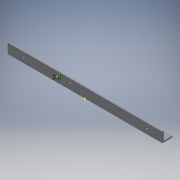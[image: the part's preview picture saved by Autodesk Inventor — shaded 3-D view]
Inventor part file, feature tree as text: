
AUTODESK INVENTOR PART (.ipt)
format: ipt  version: 2018 (Build 220112000, 112)  size: 144,896 bytes
history: native  units: mm
features: sketch x7, extrude x6, other x3, reference x2, projected_geometry x1
ambient origin geometry x8: Origin, YZ Plane, XZ Plane, XY Plane, X Axis, Y Axis, Z Axis, Center Point
bodies: Solid1 (feature_tree)
feature tree (19):
  extrude  "Extrusion1"  Depth=15.08mm
  extrude  "Extrusion2"  Depth=2.05mm
  extrude  "Extrusion3"  Depth=13.03mm
  sketch  "Sketch4"  dims[d8=93.5mm d9=8.0mm]
  extrude  "Extrusion5"  Depth=8.0mm
  extrude  "Extrusion6"  Depth=2.05mm TaperAngle=0.0deg
  extrude  "Extrusion7"  Depth=3.2mm
  sketch  "Sketch1"  dims[d0=234.5mm d1=15.08mm]
  sketch  "Sketch2"  dims[d2=2.05mm d3=0.0mm d4=2.05mm]
  sketch  "Sketch3"  dims[d5=13.03mm d6=0.0mm d7=93.5mm]
  sketch  "Sketch5"  dims[d10=8.0mm d11=2.05mm d12=0.0mm]
  sketch  "Sketch6"  dims[d13=3.2mm d14=3.2mm]
  reference  "Reference1"
  sketch  "Sketch7"  dims[d15=3.8mm d18=4.2mm d19=4.2mm d20=8.0mm d21=8.0mm d22=93.5mm d23=93.4mm d24=2.05mm d25=0.0mm d26=3.0mm d27=0.0mm d28=10.0mm d29=0.0mm]
  projected_geometry  "Projected Loop1"
  reference  "Reference2"
  other  "<userpath>\Documents\optoelectronics\CAD\Bigdriver_box\Big_housing.iam"
  other  "Big_housing.iam"
  other  "source:1"
